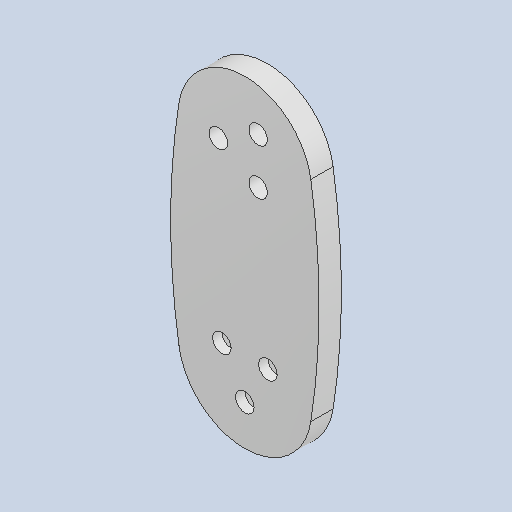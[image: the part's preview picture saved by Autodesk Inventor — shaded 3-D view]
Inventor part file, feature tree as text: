
AUTODESK INVENTOR PART (.ipt)
format: ipt  version: 2023 (Build 270158030, 158C)  size: 144,896 bytes
history: native  units: mm
features: other x3, sketch x2
ambient origin geometry x8: Origin, YZ Plane, XZ Plane, XY Plane, X Axis, Y Axis, Z Axis, Center Point
bodies: Solid1 (feature_tree)
feature tree (5):
  other  "クランク_中間.ipt"
  other  "Solid1::クランク_中間.ipt"
  other  "TaggingFeature1"
  sketch  "Sketch2"  dims[d0=10.0mm]
  sketch  "Sketch3"
